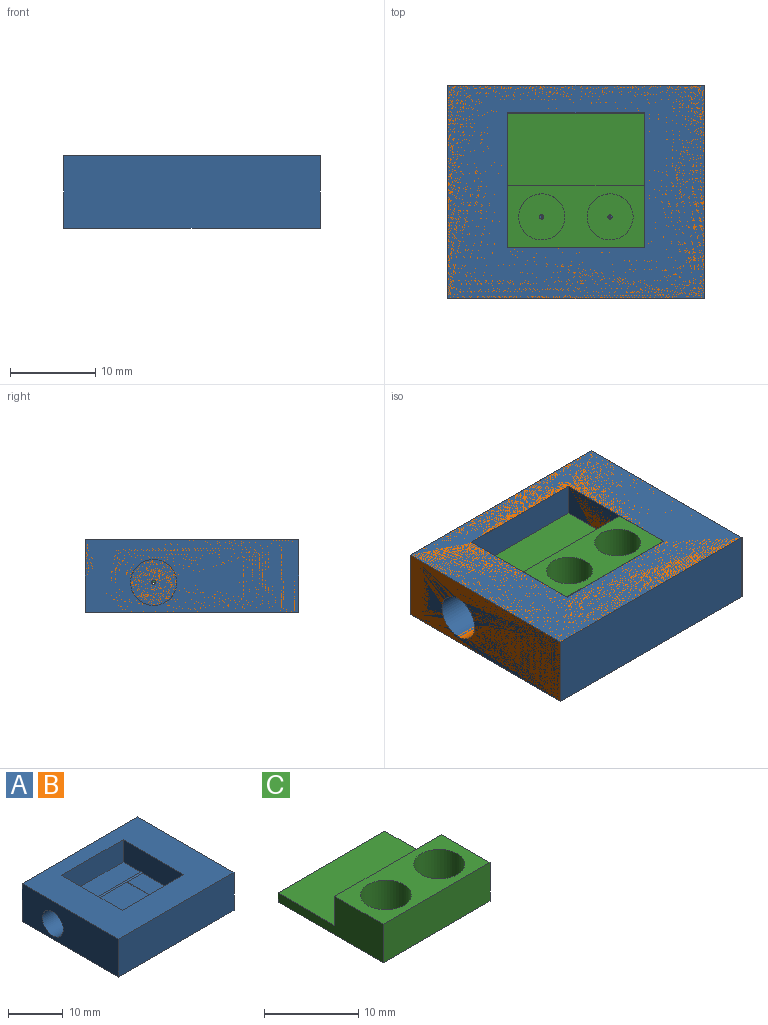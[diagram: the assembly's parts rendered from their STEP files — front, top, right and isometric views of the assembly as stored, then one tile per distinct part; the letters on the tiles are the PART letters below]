
ASSEMBLY  parts=3 mates=1
PART A: 25 faces, bbox 30x25x8.5 mm
  f0: plane 25x8.5mm, normal (1,0,0), area 189.6mm2, adj f1,f3,f8,f19,f24
  f1: plane 30x25mm, normal (0,0,1), area 498mm2, adj f0,f2,f3,f11,f12,f13,f14,f24
  f2: plane 25x8.5mm, normal (-1,0,0), area 189.6mm2, adj f1,f3,f6,f19,f24
  f3: plane 30x8.5mm, normal (0,1,0), area 255mm2, adj f0,f1,f2,f19
  f4: cylinder r=0.25mm len=18mm, axis (-1,0,0), area 15.7mm2, adj f5,f7,f9,f10,f11,f12,f15,f16
  f5: plane 5.4x5.4mm, normal (-1,0,0), area 22.7mm2, adj f4,f6
  f6: cylinder r=2.7mm len=6mm, axis (-1,0,0), area 101.8mm2, adj f2,f5
  f7: plane 5.4x5.4mm, normal (1,0,0), area 22.7mm2, adj f4,f8
  f8: cylinder r=2.7mm len=6mm, axis (1,0,0), area 101.8mm2, adj f0,f7
  f9: plane 16x4.5mm, normal (0,0,1), area 72mm2, adj f4,f11,f12,f13
  f10: plane 16x10.75mm, normal (0,0,1), area 170.8mm2, adj f4,f11,f12,f14,f15,f16,f18,f20
  f11: plane 15.75x5mm, normal (1,0,0), area 78.7mm2, adj f1,f4,f9,f10,f13,f14
  f12: plane 15.75x5mm, normal (-1,0,0), area 78.7mm2, adj f1,f4,f9,f10,f13,f14
  f13: plane 16x5mm, normal (0,-1,0), area 80mm2, adj f1,f9,f11,f12
  f14: plane 16x5mm, normal (0,1,0), area 80mm2, adj f1,f10,f11,f12
  f15: plane 8.01x0.05mm, normal (1,0,0), area 0.4mm2, adj f4,f10,f17,f18
  f16: plane 8.01x0.05mm, normal (-1,0,0), area 0.4mm2, adj f4,f10,f17,f18
  f17: plane 8.01x0.05mm, normal (0,0,1), area 0.4mm2, adj f4,f15,f16,f18
  f18: plane 0.05x0.05mm, normal (0,1,0), area 0mm2, adj f10,f15,f16,f17
  f19: plane 30x25mm, normal (0,0,-1), area 750mm2, adj f0,f2,f3,f24
  f20: plane 8.02x0.1mm, normal (1,0,0), area 0.8mm2, adj f4,f10,f22,f23
  f21: plane 8.02x0.1mm, normal (-1,0,0), area 0.8mm2, adj f4,f10,f22,f23
  f22: plane 8.02x0.1mm, normal (0,0,1), area 0.8mm2, adj f4,f20,f21,f23
  f23: plane 0.1x0.1mm, normal (0,1,0), area 0mm2, adj f10,f20,f21,f22
  f24: plane 30x8.5mm, normal (0,-1,0), area 255mm2, adj f0,f1,f2,f19
PART B: same geometry as A
PART C: 14 faces, bbox 16x15.8x5 mm
  f0: cylinder r=0.25mm len=0.5mm, axis (0,0,1), area 0.8mm2, adj f7,f12
  f1: plane 16x1.2mm, normal (0,1,0), area 19.2mm2, adj f2,f3,f7,f11
  f2: plane 15.75x5mm, normal (-1,0,0), area 46.4mm2, adj f1,f4,f6,f7,f10,f11
  f3: plane 15.75x5mm, normal (1,0,0), area 46.4mm2, adj f1,f4,f6,f7,f10,f11
  f4: plane 16x7.25mm, normal (0,0,1), area 70.2mm2, adj f2,f3,f6,f9,f10,f13
  f5: cylinder r=0.25mm len=0.5mm, axis (0,0,1), area 0.8mm2, adj f7,f8
  f6: plane 16x5mm, normal (0,-1,0), area 80mm2, adj f2,f3,f4,f7
  f7: plane 16x15.75mm, normal (0,0,-1), area 251.6mm2, adj f0,f1,f2,f3,f5,f6
  f8: plane 5.4x5.4mm, normal (0,0,1), area 22.7mm2, adj f5,f9
  f9: cylinder r=2.7mm len=5.4mm, axis (0,0,1), area 76.3mm2, adj f4,f8
  f10: plane 16x3.8mm, normal (0,1,0), area 60.8mm2, adj f2,f3,f4,f11
  f11: plane 16x8.5mm, normal (0,0,1), area 136mm2, adj f1,f2,f3,f10
  f12: plane 5.4x5.4mm, normal (0,0,1), area 22.7mm2, adj f0,f13
  f13: cylinder r=2.7mm len=5.4mm, axis (0,0,1), area 76.3mm2, adj f4,f12
PLACE A t=(4.36,-1.56,-4.35)mm
PLACE B t=(4.36,-1.55,-4.35)mm
PLACE C t=(4.35,4.8,0.65)mm
MATE fastened C.f7 <-> A.f10  axis (0,0,-1) through (4.35,4.8,0.65)mm
